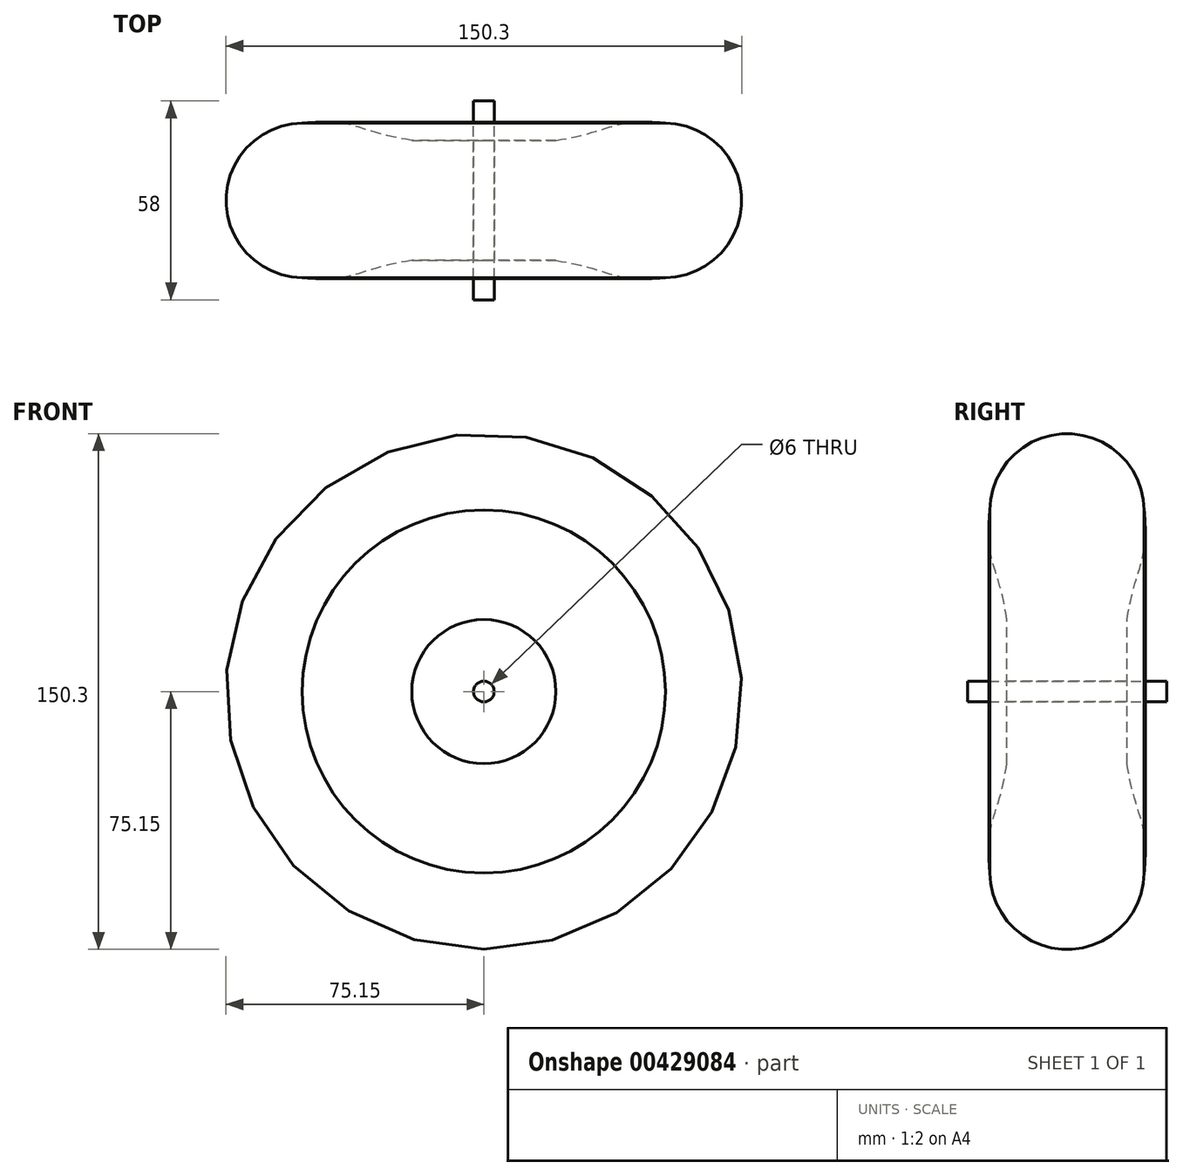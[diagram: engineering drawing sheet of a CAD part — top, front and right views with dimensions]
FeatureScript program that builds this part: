
annotation { "Feature Type Name" : "Feature", "Feature Type Description" : "" }
export const myFeature = defineFeature(function(context is Context, id is Id, definition is map)
    precondition{}
    {
        {
            var Q0;
            Q0=qCreatedBy(makeId("Top.planeOp"),FACE);
            var sketch = newSketch(context, id + "F0", { "sketchPlane" : qUnion([Q0])});
            skLineSegment(sketch, "E0.bottom", {"start": v(-3, 17.5) * mm, "end": v(-21, 17.5) * mm});
            skLineSegment(sketch, "E0.top", {"start": v(-3, -17.5) * mm, "end": v(-21, -17.5) * mm});
            skPoint(sketch, "E0.middle", {"position": v(0, 0) * mm});
            skLineSegment(sketch, "E1", {"start": v(-21, 17.5) * mm, "end": v(-75, 17.5) * mm, "construction": true});
            skLineSegment(sketch, "E2.MirrorCS", {"start": v(-21, -17.5) * mm, "end": v(-75, -17.5) * mm, "construction": true});
            skLineSegment(sketch, "E3", {"start": v(-48, 17.5) * mm, "end": v(-48, 11.94) * mm, "construction": true});
            skLineSegment(sketch, "E4", {"start": v(-48, 0) * mm, "end": v(-48, 22.5) * mm, "construction": true});
            skLineSegment(sketch, "E5", {"start": v(0, 0) * mm, "end": v(-3, 0) * mm, "construction": true});
            skLineSegment(sketch, "E6", {"start": v(-3, 0) * mm, "end": v(-3, 17.5) * mm});
            skLineSegment(sketch, "E7", {"start": v(-3, 17.5) * mm, "end": v(-3, 0) * mm});
            skLineSegment(sketch, "E8", {"start": v(-3, -17.5) * mm, "end": v(-3, 0) * mm});
            skLineSegment(sketch, "E9", {"start": v(-75.15, 0.15) * mm, "end": v(-52.91, 0) * mm, "construction": true});
            skLineSegment(sketch, "E10", {"start": v(-52.91, 0) * mm, "end": v(-52.8, 17.5) * mm, "construction": true});
            skLineSegment(sketch, "E11.MirrorCS", {"start": v(-30.67, -0.15) * mm, "end": v(-52.91, 0) * mm, "construction": true});
            skLineSegment(sketch, "E12.MirrorCS", {"start": v(-52.91, 0) * mm, "end": v(-53.03, -17.5) * mm, "construction": true});
            skLineSegment(sketch, "E13", {"start": v(-52.91, 0) * mm, "end": v(-52.91, 22.5) * mm, "construction": true});
            skLineSegment(sketch, "E14", {"start": v(-52.91, 0) * mm, "end": v(-52.91, -22.5) * mm, "construction": true});
            skArc(sketch, "E15", {"start": v(-52.91, 22.5) * mm, "mid": v(-75.15, 0) * mm, "end": v(-52.91, -22.5) * mm});
            skFitSpline(sketch, "E16", {"points": [v(-52.91, 22.5) * mm, v(-41.5, 22.5) * mm, v(-31.73, 19.86) * mm, v(-21, 17.5) * mm], "startDerivative": vector(34.25, 2.38) * mm, "endDerivative": vector(32.7, -5.06) * mm});
            skFitSpline(sketch, "E17.MirrorCS", {"points": [v(-52.91, -22.5) * mm, v(-41.5, -22.5) * mm, v(-31.73, -19.86) * mm, v(-21, -17.5) * mm], "startDerivative": vector(34.25, -2.38) * mm, "endDerivative": vector(32.7, 5.06) * mm});
            skLineSegment(sketch, "E18", {"start": v(0, 0) * mm, "end": v(0, 26.68) * mm, "construction": true});
            skSolve(sketch);
        }
        {
            var Q0;
            Q0 = qSketchRegion(id + "F0", true);
            var Q1;
            Q1=sQuery(id+"F0.wireOp",EDGE,"E18");
            revolve(context, id + "F1", {"entities" : qUnion([Q0]), "axis" : qUnion([Q1]), "revolveType" : RevolveType.FULL});
        }
        {
            var Q0;
            Q0=qCreatedBy(makeId("Front.planeOp"),FACE);
            var sketch = newSketch(context, id + "F2", { "sketchPlane" : qUnion([Q0])});
            skCircle(sketch, "E19", {"center": v(0, 0) * mm, "radius": 3 * mm});
            skSolve(sketch);
        }
        {
            var Q0;
            Q0 = qSketchRegion(id + "F2", true);
            extrude(context, id + "F3", {"entities" : qUnion([Q0]), "endBound" : BoundingType.SYMMETRIC, "depth" : 58 * mm});
        }
    });
